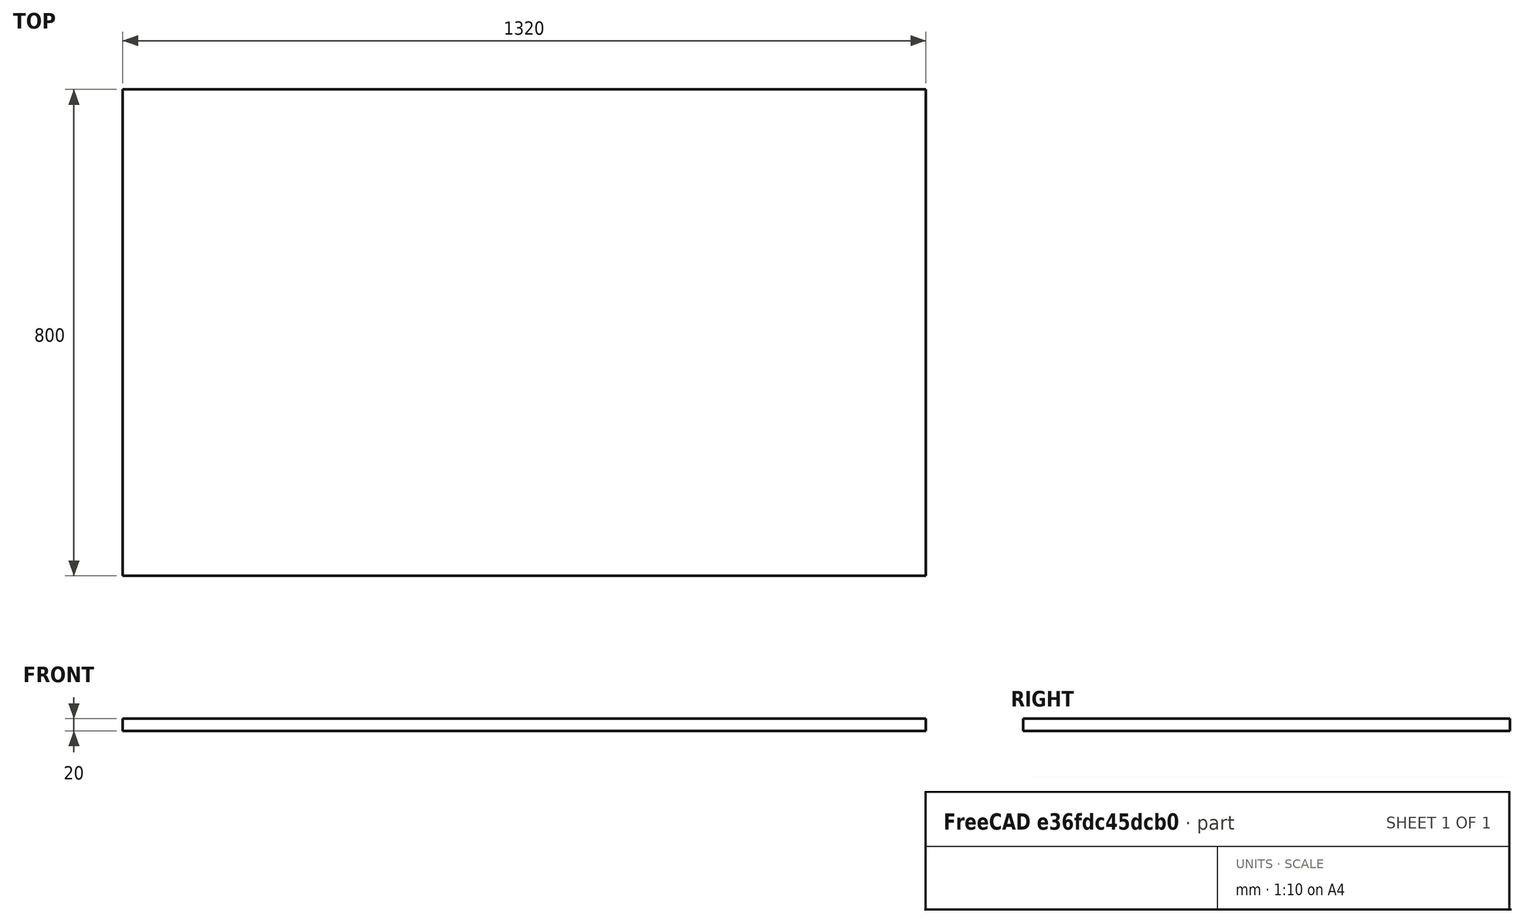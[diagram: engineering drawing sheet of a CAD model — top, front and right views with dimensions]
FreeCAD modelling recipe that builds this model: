
FCSTD DOCUMENT  (FreeCAD 0.20R29603 (Git))
Label: PlatteObenSchraeg
License: All rights reserved
LicenseURL: http://en.wikipedia.org/wiki/All_rights_reserved
objects: Sketcher::SketchObject×1, PartDesign::Pad×1, PartDesign::Body×1
note: 4 computed .brp shape members not serialized (recipe doc carries the construction recipe); baked Part::Feature solids carry a one-line shape summary decoded from their .brp

FEATURE [Sketcher::SketchObject] Sketch
  FullyConstrained = true
  MapMode = 5
  Support = -> [XY_Plane]
  sketch-geometry (5):
    g0: LineSegment StartX=-660 StartY=400 StartZ=0 EndX=-660 EndY=-400 EndZ=0
    g1: LineSegment StartX=-660 StartY=-400 StartZ=0 EndX=660 EndY=-400 EndZ=0
    g2: LineSegment StartX=660 StartY=-400 StartZ=0 EndX=660 EndY=400 EndZ=0
    g3: LineSegment StartX=660 StartY=400 StartZ=0 EndX=-660 EndY=400 EndZ=0
    g4: GeomPoint X=0 Y=0 Z=0
  constraints (12):
    c: Coincident(g0,g1)
    c: Coincident(g1,g2)
    c: Coincident(g2,g3)
    c: Coincident(g3,g0)
    c: Horizontal(g1)
    c: Horizontal(g3)
    c: Vertical(g0)
    c: Vertical(g2)
    c: Symmetric(g1,g0,g4)
    c: Coincident(g4,g-1)
    c: Distance(g3) = 1320
    c: Distance(g0) = 800
FEATURE [PartDesign::Pad] Pad
  Direction = (0,0,1)
  Length = 20
  Length2 = 10
  Profile = -> Sketch
  ReferenceAxis = -> Sketch [N_Axis]
  Type = 0
FEATURE [PartDesign::Body] Body
  Group = -> [Sketch,Pad]
  Origin = -> Origin
  Tip = -> Pad
